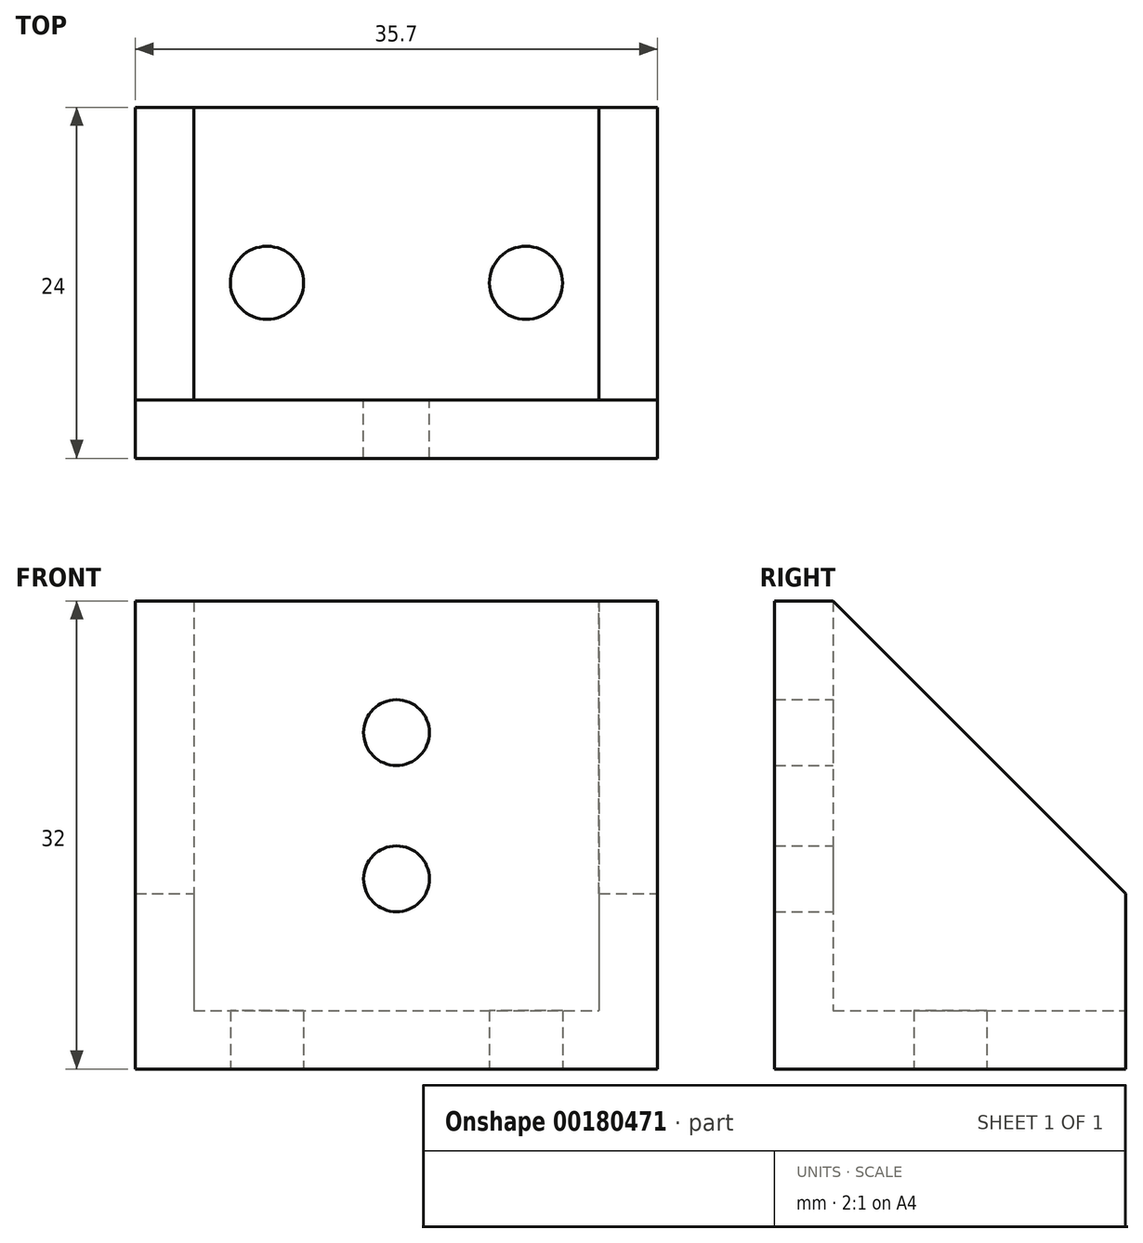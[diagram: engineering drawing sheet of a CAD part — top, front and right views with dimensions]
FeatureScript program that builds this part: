
annotation { "Feature Type Name" : "Feature", "Feature Type Description" : "" }
export const myFeature = defineFeature(function(context is Context, id is Id, definition is map)
    precondition{}
    {
        {
            var Q0;
            Q0=qCreatedBy(makeId("Top.planeOp"),FACE);
            var sketch = newSketch(context, id + "F0", { "sketchPlane" : qUnion([Q0])});
            skLineSegment(sketch, "E0.bottom", {"start": v(0, 0) * mm, "end": v(35.7, 0) * mm});
            skLineSegment(sketch, "E0.top", {"start": v(0, 24) * mm, "end": v(35.7, 24) * mm});
            skLineSegment(sketch, "E0.left", {"start": v(0, 0) * mm, "end": v(0, 24) * mm});
            skLineSegment(sketch, "E0.right", {"start": v(35.7, 0) * mm, "end": v(35.7, 24) * mm});
            skCircle(sketch, "E1", {"center": v(9, 12) * mm, "radius": 2.5 * mm});
            skCircle(sketch, "E2", {"center": v(26.7, 12) * mm, "radius": 2.5 * mm});
            skSolve(sketch);
        }
        {
            var Q0;
            Q0=makeQuery(id+"F0.imprint","IMPRINT",FACE,{"disambiguationData":[TD([[makeQuery(id+"F0.imprint","IMPRINT",EDGE,{"derivedFrom":sQuery(id+"F0.wireOp",EDGE,"E0.bottom")}),1.0]])]});
            extrude(context, id + "F1", {"entities" : qUnion([Q0]), "depth" : 4 * mm});
        }
        {
            var Q0;
            Q0=makeQuery(id+"F1.opExtrude","CAP_FACE",FACE,{"disambiguationData":[OSD([sQuery(id+"F0.wireOp",EDGE,"E0.bottom"),sQuery(id+"F0.wireOp",EDGE,"E0.top"),sQuery(id+"F0.wireOp",EDGE,"E0.left"),sQuery(id+"F0.wireOp",EDGE,"E0.right"),sQuery(id+"F0.wireOp",EDGE,"E1"),sQuery(id+"F0.wireOp",EDGE,"E2")])],"isStart":false});
            var sketch = newSketch(context, id + "F2", { "sketchPlane" : qUnion([Q0])});
            skLineSegment(sketch, "E3.0", {"start": v(4, 4) * mm, "end": v(31.7, 4) * mm});
            skLineSegment(sketch, "E3.1", {"start": v(4, 4) * mm, "end": v(4, 20) * mm});
            skLineSegment(sketch, "E3.3", {"start": v(31.7, 4) * mm, "end": v(31.7, 20) * mm});
            skLineSegment(sketch, "E4", {"start": v(4, 20) * mm, "end": v(4, 24) * mm});
            skLineSegment(sketch, "E5", {"start": v(31.7, 20) * mm, "end": v(31.7, 24) * mm});
            skSolve(sketch);
        }
        {
            var Q0;
            Q0=makeQuery(id+"F2.imprint","IMPRINT",FACE,{"disambiguationData":[TD([[makeQuery(id+"F2.imprint","IMPRINT",EDGE,{"derivedFrom":sQuery(id+"F2.wireOp",EDGE,"E3.0")}),-1.0]])]});
            extrude(context, id + "F3", {"entities" : qUnion([Q0]), "operationType" : NewBodyOperationType.ADD, "depth" : 28 * mm});
        }
        {
            var Q0;
            {var subQ0=sQuery(id+"F0.wireOp",EDGE,"E0.top");var subQ1=makeQuery(id+"F1.opExtrude","CAP_EDGE",EDGE,{"disambiguationData":[OSD([subQ0])],"isStart":false});Q0=makeQuery(id+"F3.opExtrude","CAP_EDGE",EDGE,{"disambiguationData":[OSD([subQ0]),TDD([makeQuery(id+"F2.imprint","IMPRINT",EDGE,{"disambiguationData":[TD([[makeQuery(id+"F2.imprint","INTERSECT",VERTEX,{"derivedFrom":[subQ1,makeQuery(id+"F1.opExtrude","CAP_EDGE",EDGE,{"disambiguationData":[OSD([sQuery(id+"F0.wireOp",EDGE,"E0.right")])],"isStart":false})]}),1.0]])],"derivedFrom":subQ1})])],"isStart":false});}
            var Q1;
            {var subQ0=sQuery(id+"F0.wireOp",EDGE,"E0.top");var subQ1=makeQuery(id+"F1.opExtrude","CAP_EDGE",EDGE,{"disambiguationData":[OSD([subQ0])],"isStart":false});Q1=makeQuery(id+"F3.opExtrude","CAP_EDGE",EDGE,{"disambiguationData":[OSD([subQ0]),TDD([makeQuery(id+"F2.imprint","IMPRINT",EDGE,{"disambiguationData":[TD([[makeQuery(id+"F2.imprint","INTERSECT",VERTEX,{"derivedFrom":[subQ1,makeQuery(id+"F1.opExtrude","CAP_EDGE",EDGE,{"disambiguationData":[OSD([sQuery(id+"F0.wireOp",EDGE,"E0.left")])],"isStart":false})]}),-1.0]])],"derivedFrom":subQ1})])],"isStart":false});}
            chamfer(context, id + "F4", {"entities" : qUnion([Q0, Q1]), "width" : 20 * mm, "tangentPropagation" : true});
        }
        {
            var Q0;
            Q0=makeQuery(id+"F3.opExtrude","SWEPT_FACE",FACE,{"disambiguationData":[OSD([sQuery(id+"F2.wireOp",EDGE,"E3.0")])]});
            var sketch = newSketch(context, id + "F5", { "sketchPlane" : qUnion([Q0])});
            skCircle(sketch, "E6", {"center": v(-17.85, 23) * mm, "radius": 2.25 * mm});
            skCircle(sketch, "E7", {"center": v(-17.85, 13) * mm, "radius": 2.25 * mm});
            skSolve(sketch);
        }
        {
            var Q0;
            Q0=makeQuery(id+"F5.imprint","IMPRINT",FACE,{"disambiguationData":[TD([[makeQuery(id+"F5.imprint","IMPRINT",EDGE,{"derivedFrom":sQuery(id+"F5.wireOp",EDGE,"E6")}),1.0]])]});
            var Q1;
            Q1=makeQuery(id+"F5.imprint","IMPRINT",FACE,{"disambiguationData":[TD([[makeQuery(id+"F5.imprint","IMPRINT",EDGE,{"derivedFrom":sQuery(id+"F5.wireOp",EDGE,"E7")}),1.0]])]});
            extrude(context, id + "F6", {"entities" : qUnion([Q0, Q1]), "operationType" : NewBodyOperationType.REMOVE, "oppositeDirection" : true, "depth" : 4 * mm});
        }
    });
